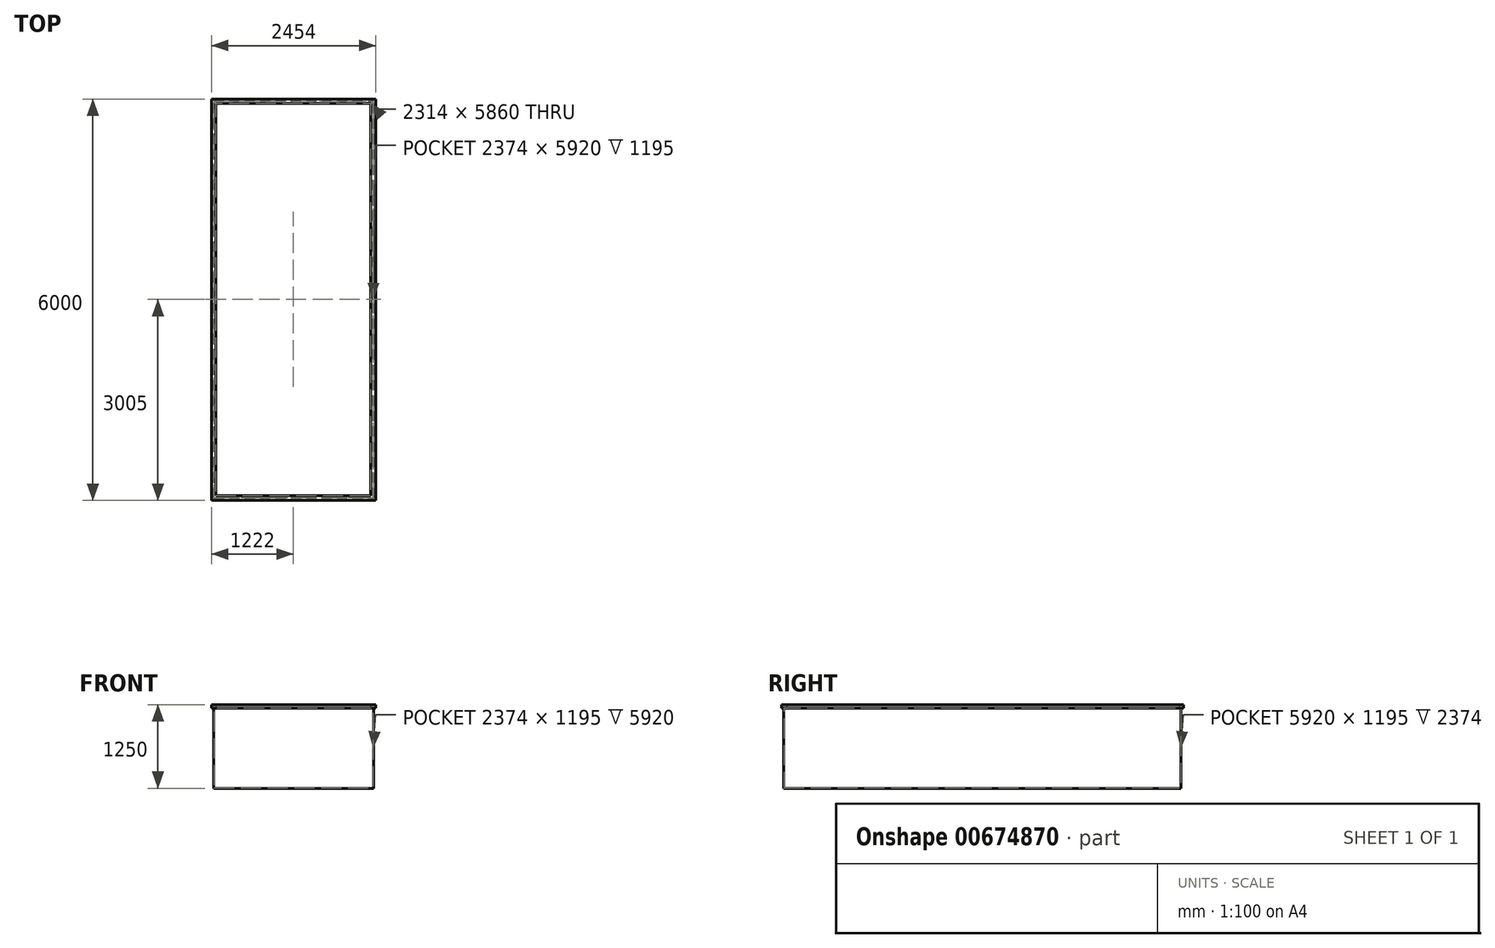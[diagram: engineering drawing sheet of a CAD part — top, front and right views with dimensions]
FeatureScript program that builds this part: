
annotation { "Feature Type Name" : "Feature", "Feature Type Description" : "" }
export const myFeature = defineFeature(function(context is Context, id is Id, definition is map)
    precondition{}
    {
        {
            var Q0;
            Q0=qCreatedBy(makeId("Top.planeOp"),FACE);
            var sketch = newSketch(context, id + "F0", { "sketchPlane" : qUnion([Q0])});
            skLineSegment(sketch, "E0.bottom", {"start": v(0, 0) * mm, "end": v(2384, 0) * mm});
            skLineSegment(sketch, "E0.top", {"start": v(0, 5930) * mm, "end": v(2384, 5930) * mm});
            skLineSegment(sketch, "E0.left", {"start": v(0, 0) * mm, "end": v(0, 5930) * mm});
            skLineSegment(sketch, "E0.right", {"start": v(2384, 0) * mm, "end": v(2384, 5930) * mm});
            skSolve(sketch);
        }
        {
            var Q0;
            Q0=makeQuery(id+"F0.imprint","IMPRINT",FACE,{"disambiguationData":[TD([[makeQuery(id+"F0.imprint","IMPRINT",EDGE,{"derivedFrom":sQuery(id+"F0.wireOp",EDGE,"E0.bottom")}),1.0]])]});
            extrude(context, id + "F1", {"entities" : qUnion([Q0]), "depth" : 1200 * mm, "offsetDistance" : 25 * mm});
        }
        {
            var Q0;
            Q0=makeQuery(id+"F1.opExtrude","CAP_FACE",FACE,{"disambiguationData":[OSD([sQuery(id+"F0.wireOp",EDGE,"E0.bottom"),sQuery(id+"F0.wireOp",EDGE,"E0.top"),sQuery(id+"F0.wireOp",EDGE,"E0.left"),sQuery(id+"F0.wireOp",EDGE,"E0.right")])],"isStart":false});
            shell(context, id + "F2", {"entities" : qUnion([Q0]), "thickness" : 5 * mm});
        }
        {
            var Q0;
            Q0=makeQuery(id+"F1.opExtrude","CAP_FACE",FACE,{"disambiguationData":[OSD([sQuery(id+"F0.wireOp",EDGE,"E0.bottom"),sQuery(id+"F0.wireOp",EDGE,"E0.top"),sQuery(id+"F0.wireOp",EDGE,"E0.left"),sQuery(id+"F0.wireOp",EDGE,"E0.right")])],"isStart":false});
            var sketch = newSketch(context, id + "F3", { "sketchPlane" : qUnion([Q0])});
            skLineSegment(sketch, "E1.bottom", {"start": v(-35, 5965) * mm, "end": v(2419, 5965) * mm});
            skLineSegment(sketch, "E1.top", {"start": v(-35, -35) * mm, "end": v(2419, -35) * mm});
            skLineSegment(sketch, "E1.left", {"start": v(-35, 5965) * mm, "end": v(-35, -35) * mm});
            skLineSegment(sketch, "E1.right", {"start": v(2419, 5965) * mm, "end": v(2419, -35) * mm});
            skLineSegment(sketch, "E2.bottom", {"start": v(30, 5900) * mm, "end": v(2344, 5900) * mm});
            skLineSegment(sketch, "E2.top", {"start": v(30, 40) * mm, "end": v(2344, 40) * mm});
            skLineSegment(sketch, "E2.left", {"start": v(30, 5900) * mm, "end": v(30, 40) * mm});
            skLineSegment(sketch, "E2.right", {"start": v(2344, 5900) * mm, "end": v(2344, 40) * mm});
            skSolve(sketch);
        }
        {
            var Q0;
            Q0 = qSketchRegion(id + "F3", true);
            extrude(context, id + "F4", {"entities" : qUnion([Q0]), "operationType" : NewBodyOperationType.ADD, "depth" : 50 * mm, "offsetDistance" : 25 * mm});
        }
    });
